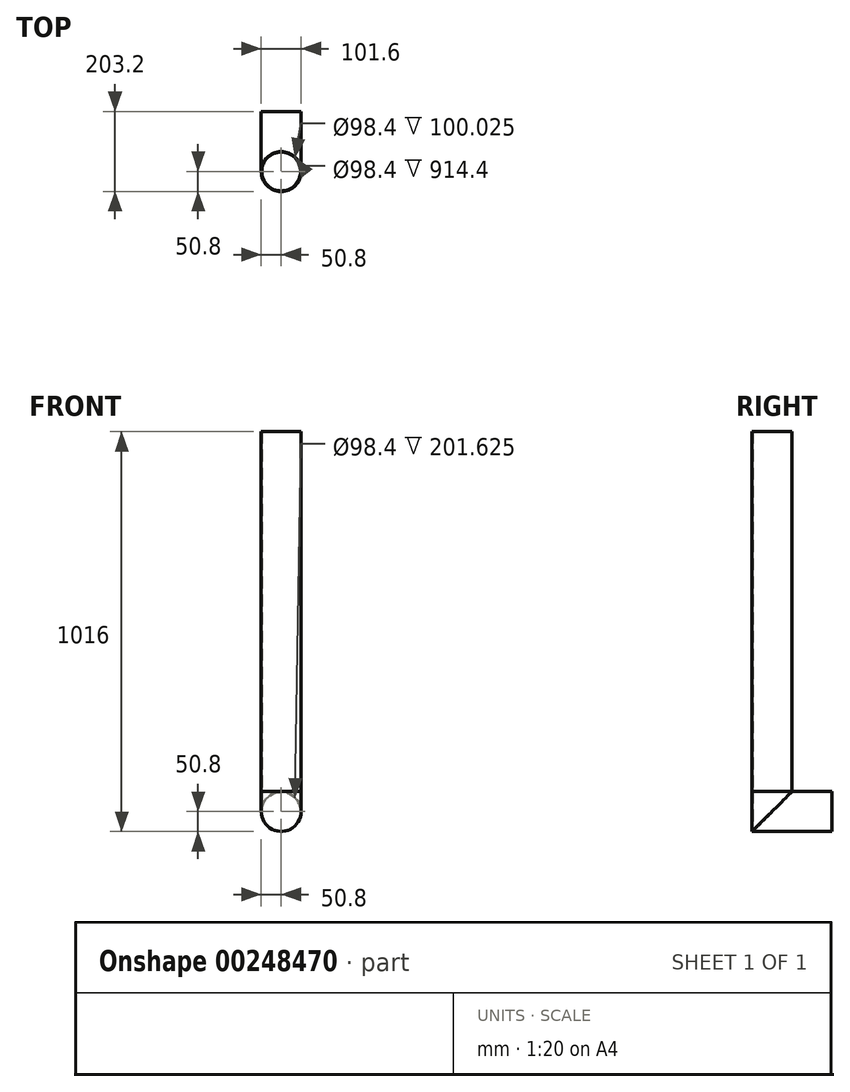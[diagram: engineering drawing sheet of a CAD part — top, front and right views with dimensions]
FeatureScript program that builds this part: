
annotation { "Feature Type Name" : "Feature", "Feature Type Description" : "" }
export const myFeature = defineFeature(function(context is Context, id is Id, definition is map)
    precondition{}
    {
        {
            var Q0;
            Q0=qCreatedBy(makeId("Top.planeOp"),FACE);
            var sketch = newSketch(context, id + "F0", { "sketchPlane" : qUnion([Q0])});
            skCircle(sketch, "E0", {"center": v(0, 0) * mm, "radius": 49.2 * mm});
            skCircle(sketch, "E1", {"center": v(0, 0) * mm, "radius": 50.8 * mm});
            skSolve(sketch);
        }
        {
            var Q0;
            Q0=makeQuery(id+"F0.imprint","IMPRINT",FACE,{"disambiguationData":[TD([[makeQuery(id+"F0.imprint","IMPRINT",EDGE,{"derivedFrom":sQuery(id+"F0.wireOp",EDGE,"E0")}),-1.0]])]});
            extrude(context, id + "F1", {"entities" : qUnion([Q0]), "depth" : 914.4 * mm});
        }
        {
            var Q0;
            Q0=qCreatedBy(makeId("Right.planeOp"),FACE);
            var sketch = newSketch(context, id + "F2", { "sketchPlane" : qUnion([Q0])});
            skLineSegment(sketch, "E2", {"start": v(0, 0) * mm, "end": v(0, -50.8) * mm});
            skLineSegment(sketch, "E3", {"start": v(0, -50.8) * mm, "end": v(152.4, -50.8) * mm});
            skSolve(sketch);
        }
        {
            var Q0;
            Q0=makeQuery(id+"F0.imprint","IMPRINT",FACE,{"disambiguationData":[TD([[makeQuery(id+"F0.imprint","IMPRINT",EDGE,{"derivedFrom":sQuery(id+"F0.wireOp",EDGE,"E0")}),-1.0]])]});
            var Q1;
            Q1=sQuery(id+"F0.wireOp",EDGE,"E1");
            var Q2;
            Q2=sQuery(id+"F0.wireOp",EDGE,"E0");
            var Q3;
            Q3=sQuery(id+"F2.wireOp",EDGE,"E2");
            var Q4;
            Q4=sQuery(id+"F2.wireOp",EDGE,"E3");
            sweep(context, id + "F3", {"profiles" : qUnion([Q0]), "surfaceProfiles" : qUnion([Q1, Q2]), "path" : qUnion([Q3, Q4])});
        }
    });
